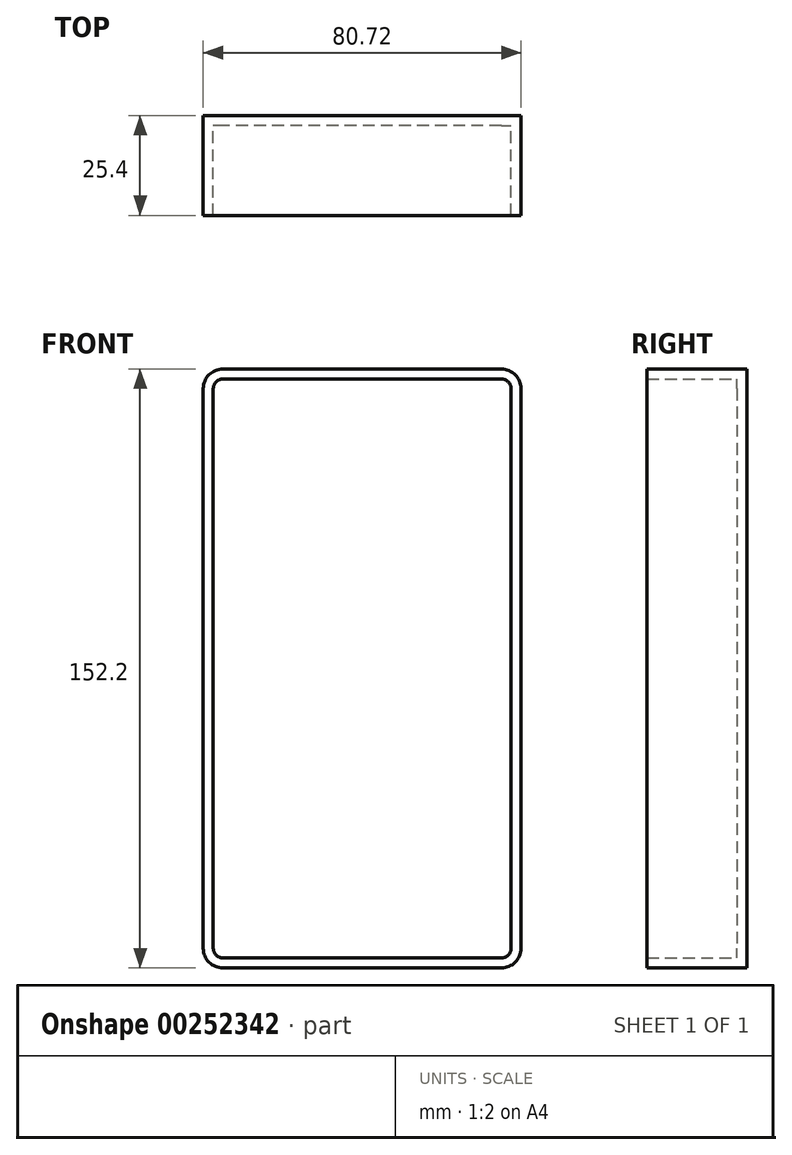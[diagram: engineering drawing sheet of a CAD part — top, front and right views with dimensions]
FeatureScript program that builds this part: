
annotation { "Feature Type Name" : "Feature", "Feature Type Description" : "" }
export const myFeature = defineFeature(function(context is Context, id is Id, definition is map)
    precondition{}
    {
        {
            var Q0;
            Q0=qCreatedBy(makeId("Front.planeOp"),FACE);
            var sketch = newSketch(context, id + "F0", { "sketchPlane" : qUnion([Q0])});
            skLineSegment(sketch, "E0.bottom", {"start": v(40.36, 76.1) * mm, "end": v(-40.36, 76.1) * mm});
            skLineSegment(sketch, "E0.top", {"start": v(40.36, -76.1) * mm, "end": v(-40.36, -76.1) * mm});
            skLineSegment(sketch, "E0.left", {"start": v(40.36, 76.1) * mm, "end": v(40.36, -76.1) * mm});
            skLineSegment(sketch, "E0.right", {"start": v(-40.36, 76.1) * mm, "end": v(-40.36, -76.1) * mm});
            skPoint(sketch, "E0.middle", {"position": v(0, 0) * mm});
            skSolve(sketch);
        }
        {
            var Q0;
            Q0=makeQuery(id+"F0.imprint","IMPRINT",FACE,{"disambiguationData":[TD([[makeQuery(id+"F0.imprint","IMPRINT",EDGE,{"derivedFrom":sQuery(id+"F0.wireOp",EDGE,"E0.bottom")}),1.0]])]});
            extrude(context, id + "F1", {"entities" : qUnion([Q0]), "endBound" : BoundingType.SYMMETRIC, "depth" : 25.4 * mm});
        }
        {
            var Q0;
            Q0=makeQuery(id+"F1.opExtrude","SWEPT_EDGE",EDGE,{"disambiguationData":[OSD([sQuery(id+"F0.wireOp",EDGE,"E0.bottom"),sQuery(id+"F0.wireOp",EDGE,"E0.right")])]});
            var Q1;
            Q1=makeQuery(id+"F1.opExtrude","SWEPT_EDGE",EDGE,{"disambiguationData":[OSD([sQuery(id+"F0.wireOp",EDGE,"E0.bottom"),sQuery(id+"F0.wireOp",EDGE,"E0.left")])]});
            var Q2;
            Q2=makeQuery(id+"F1.opExtrude","SWEPT_EDGE",EDGE,{"disambiguationData":[OSD([sQuery(id+"F0.wireOp",EDGE,"E0.top"),sQuery(id+"F0.wireOp",EDGE,"E0.left")])]});
            var Q3;
            Q3=makeQuery(id+"F1.opExtrude","SWEPT_EDGE",EDGE,{"disambiguationData":[OSD([sQuery(id+"F0.wireOp",EDGE,"E0.top"),sQuery(id+"F0.wireOp",EDGE,"E0.right")])]});
            fillet(context, id + "F2", {"entities" : qUnion([Q0, Q1, Q2, Q3]), "radius" : 5 * mm, "tangentPropagation" : true, "allowEdgeOverflow" : false});
        }
        {
            var Q0;
            Q0=makeQuery(id+"F1.opExtrude","CAP_FACE",FACE,{"disambiguationData":[OSD([sQuery(id+"F0.wireOp",EDGE,"E0.bottom"),sQuery(id+"F0.wireOp",EDGE,"E0.top"),sQuery(id+"F0.wireOp",EDGE,"E0.left"),sQuery(id+"F0.wireOp",EDGE,"E0.right")])],"isStart":false});
            shell(context, id + "F3", {"entities" : qUnion([Q0]), "thickness" : 2.54 * mm});
        }
    });
